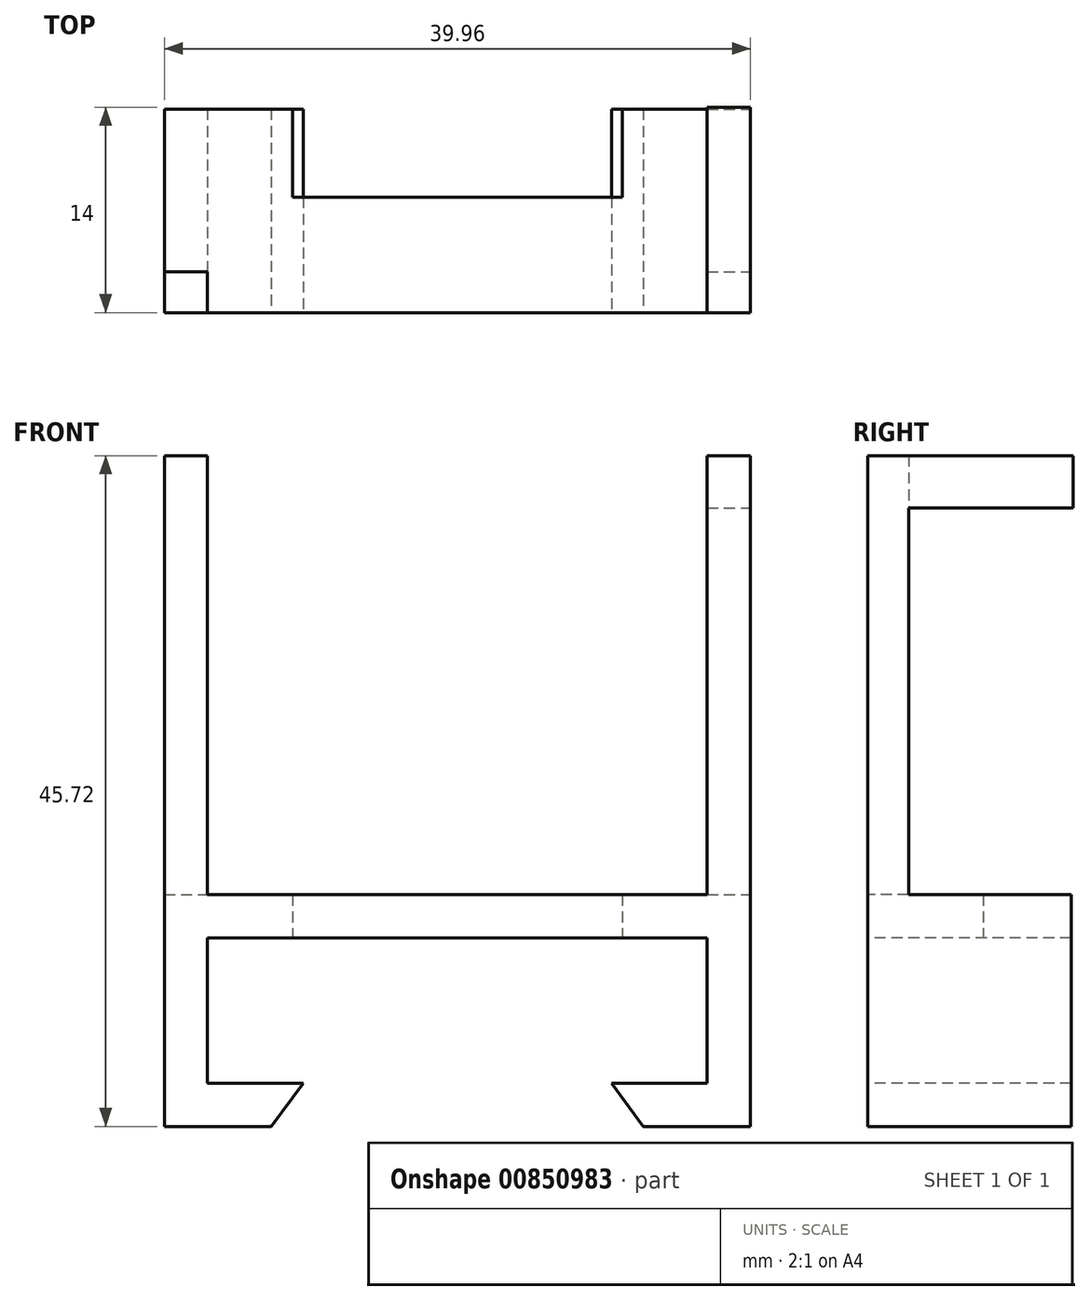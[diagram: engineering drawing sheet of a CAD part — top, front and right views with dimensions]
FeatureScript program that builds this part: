
annotation { "Feature Type Name" : "Feature", "Feature Type Description" : "" }
export const myFeature = defineFeature(function(context is Context, id is Id, definition is map)
    precondition{}
    {
        {
            var Q0;
            Q0=qCreatedBy(makeId("Front.planeOp"),FACE);
            var sketch = newSketch(context, id + "F0", { "sketchPlane" : qUnion([Q0])});
            skLineSegment(sketch, "E0", {"start": v(32.66, 29.92) * mm, "end": v(32.66, 0) * mm});
            skLineSegment(sketch, "E1", {"start": v(32.66, 29.92) * mm, "end": v(29.71, 29.92) * mm});
            skLineSegment(sketch, "E2", {"start": v(-4.35, 29.92) * mm, "end": v(-4.35, 26.37) * mm});
            skLineSegment(sketch, "E3", {"start": v(-4.35, 26.37) * mm, "end": v(-4.35, 29.92) * mm});
            skLineSegment(sketch, "E4", {"start": v(-4.35, 29.92) * mm, "end": v(-7.3, 29.92) * mm});
            skLineSegment(sketch, "E5", {"start": v(-7.3, 29.92) * mm, "end": v(-7.3, 0) * mm});
            skLineSegment(sketch, "E6", {"start": v(-7.3, 29.92) * mm, "end": v(-7.3, 26.37) * mm});
            skLineSegment(sketch, "E7", {"start": v(-7.3, 26.37) * mm, "end": v(-4.35, 26.37) * mm});
            skLineSegment(sketch, "E8", {"start": v(32.66, 29.92) * mm, "end": v(32.66, 26.37) * mm});
            skLineSegment(sketch, "E9", {"start": v(32.66, 26.37) * mm, "end": v(29.67, 26.37) * mm});
            skLineSegment(sketch, "E10", {"start": v(29.71, 29.92) * mm, "end": v(29.71, 26.37) * mm});
            skLineSegment(sketch, "E11", {"start": v(29.71, 26.37) * mm, "end": v(29.71, 0) * mm});
            skLineSegment(sketch, "E12", {"start": v(-4.35, 26.37) * mm, "end": v(-4.35, 0) * mm});
            skLineSegment(sketch, "E13", {"start": v(-4.35, 0) * mm, "end": v(29.71, 0) * mm});
            skLineSegment(sketch, "E14", {"start": v(-7.3, 0) * mm, "end": v(-4.35, 0) * mm});
            skLineSegment(sketch, "E15", {"start": v(29.71, 0) * mm, "end": v(32.66, 0) * mm});
            skLineSegment(sketch, "E16", {"start": v(29.71, -2.95) * mm, "end": v(-4.35, -2.95) * mm});
            skLineSegment(sketch, "E17", {"start": v(-4.35, -2.95) * mm, "end": v(-4.35, -12.85) * mm});
            skLineSegment(sketch, "E18", {"start": v(-7.3, 0) * mm, "end": v(-7.3, -15.8) * mm});
            skLineSegment(sketch, "E19", {"start": v(32.66, -15.8) * mm, "end": v(32.66, 0) * mm});
            skLineSegment(sketch, "E20", {"start": v(-7.3, 0) * mm, "end": v(1.44, 0) * mm});
            skLineSegment(sketch, "E21", {"start": v(32.66, 0) * mm, "end": v(23.92, 0) * mm});
            skLineSegment(sketch, "E22", {"start": v(1.44, 0) * mm, "end": v(1.44, -2.95) * mm});
            skLineSegment(sketch, "E23", {"start": v(23.92, 0) * mm, "end": v(23.92, -2.95) * mm});
            skLineSegment(sketch, "E24", {"start": v(-4.35, -12.85) * mm, "end": v(2.18, -12.85) * mm});
            skLineSegment(sketch, "E25", {"start": v(29.71, -2.95) * mm, "end": v(29.71, -12.85) * mm});
            skLineSegment(sketch, "E26", {"start": v(29.71, -15.8) * mm, "end": v(32.66, -15.8) * mm});
            skLineSegment(sketch, "E27", {"start": v(-4.35, -15.8) * mm, "end": v(-7.3, -15.8) * mm});
            skPoint(sketch, "E28.end.orphan", {"position": v(0, -15.8) * mm});
            skLineSegment(sketch, "E29", {"start": v(29.71, -15.8) * mm, "end": v(25.37, -15.8) * mm});
            skLineSegment(sketch, "E30", {"start": v(-4.35, -15.8) * mm, "end": v(0, -15.8) * mm});
            skLineSegment(sketch, "E31.trimOffspring", {"start": v(23.18, -12.85) * mm, "end": v(29.71, -12.85) * mm});
            skLineSegment(sketch, "E32", {"start": v(2.18, -12.85) * mm, "end": v(0, -15.8) * mm});
            skLineSegment(sketch, "E33", {"start": v(32.66, -15.8) * mm, "end": v(25.37, -15.8) * mm});
            skLineSegment(sketch, "E34", {"start": v(25.37, -15.8) * mm, "end": v(23.18, -12.85) * mm});
            skSolve(sketch);
        }
        {
            var Q0;
            Q0=makeQuery(id+"F0.imprint","IMPRINT",FACE,{"disambiguationData":[TD([[makeQuery(id+"F0.imprint","IMPRINT",EDGE,{"derivedFrom":sQuery(id+"F0.wireOp",EDGE,"E3")}),1.0]])]});
            var Q1;
            Q1=makeQuery(id+"F0.imprint","IMPRINT",FACE,{"disambiguationData":[TD([[makeQuery(id+"F0.imprint","IMPRINT",EDGE,{"derivedFrom":sQuery(id+"F0.wireOp",EDGE,"E1")}),1.0]])]});
            extrude(context, id + "F1", {"entities" : qUnion([Q0, Q1]), "oppositeDirection" : true, "depth" : 14 * mm, "offsetDistance" : 25.4 * mm});
        }
        {
            var Q0;
            {var subQ0=sQuery(id+"F0.wireOp",EDGE,"E5");Q0=makeQuery(id+"F0.imprint","IMPRINT",FACE,{"disambiguationData":[TD([[makeQuery(id+"F0.imprint","IMPRINT",EDGE,{"derivedFrom":subQ0}),1.0]])]});}
            var Q1;
            {var subQ0=sQuery(id+"F0.wireOp",EDGE,"E0");Q1=makeQuery(id+"F0.imprint","IMPRINT",FACE,{"disambiguationData":[TD([[makeQuery(id+"F0.imprint","IMPRINT",EDGE,{"derivedFrom":subQ0}),-1.0]])]});}
            extrude(context, id + "F2", {"entities" : qUnion([Q0, Q1]), "operationType" : NewBodyOperationType.ADD, "oppositeDirection" : true, "depth" : 2.8 * mm, "offsetDistance" : 25.4 * mm});
        }
        {
            var Q0;
            {var subQ1=sQuery(id+"F0.wireOp",EDGE,"E19");Q0=makeQuery(id+"F0.imprint","IMPRINT",FACE,{"disambiguationData":[TD([[makeQuery(id+"F0.imprint","IMPRINT",EDGE,{"derivedFrom":subQ1}),1.0]])]});}
            var Q1;
            {var subQ1=sQuery(id+"F0.wireOp",EDGE,"E18");Q1=makeQuery(id+"F0.imprint","IMPRINT",FACE,{"disambiguationData":[TD([[makeQuery(id+"F0.imprint","IMPRINT",EDGE,{"derivedFrom":subQ1}),1.0]])]});}
            extrude(context, id + "F3", {"entities" : qUnion([Q0, Q1]), "operationType" : NewBodyOperationType.ADD, "oppositeDirection" : true, "depth" : 13.87 * mm, "offsetDistance" : 25.4 * mm});
        }
        {
            var Q0;
            Q0=makeQuery(id+"F0.imprint","IMPRINT",FACE,{"disambiguationData":[TD([[makeQuery(id+"F0.imprint","IMPRINT",EDGE,{"derivedFrom":sQuery(id+"F0.wireOp",EDGE,"E13")}),-1.0]])]});
            extrude(context, id + "F4", {"entities" : qUnion([Q0]), "operationType" : NewBodyOperationType.ADD, "oppositeDirection" : true, "depth" : 7.87 * mm, "offsetDistance" : 25.4 * mm});
        }
    });
